# Revit family: Hager-WITTY ONE WALL MOUNTED-fr-BE-BE
name_source: partatom
category: Electrical Fixtures
units: mm (PartAtom-declared; Revit-internal decimal feet)

## family parameters
Always vertical = Yes
Cut with Voids When Loaded = No
Host = Wall
Maintain Annotation Orientation = No
OmniClass Number = 23.75.00.00
OmniClass Title = Climate Control (HVAC)
Part Type = Normal
Room Calculation Point = No
Round Connector Dimension = Use Diameter
Shared = No

## types (2) — shared parameters
BC_METADATA = {"ObjectGuid":"b7395028-ef9e-46b8-b49f-e0fe9c8fa070","ModelGuid":"b1efb829-c177-4a88-8b0d-f632edc25d22","VariantGuid":"c7b0c534-fef0-4725-a2d6-e8a658ebdb92","Revision":"#2","VariantName":"REF 1"}
BC_MODEL_ID = 1528865
BC_OBJECT_ID = 511137
BC_OBJECT_VERSION = #1
Code hager = ADD_EC002883_ECVS_WO
EF000003 - Type de montage = Montage mural
EF000008 - Largeur = 250 mm  [stored 0.82021 ft]
EF000040 - Hauteur = 370 mm  [stored 1.21391 ft]
EF000049 - Profondeur = 150 mm  [stored 0.492126 ft]
EF000458 - Avec affichage = No
EF001596 - Matériau du boîtier = Plastique
EF002136 - Puissance de raccordement nominale = 11000 W
EF003840 - Tension d'entrée = 400 V
EF004293 - Résistance aux chocs = IK08
EF005455 - Fréquence = 50/60 Hz
EF005474 - Classe de protection (IP) = IP54
EF007001 - Tension de sortie CC = 0 V
EF007353 - Courant de sortie max. CC = 0 A
EF009078 - Nombre de points de chargement = 1
EF009089 - Avec boîte de raccordement domestique = No
EF009300 - Puissance max. par point de chargement = 11000 W
EF009305 - Nombre de prises de charge type 2 = 1
EF009313 - Avec compteur d'énergie = No
EF009314 - Avec disjoncteur de protection = No
EF009547 - LTE = No
EF011072 - Compatible IFTTT = No
EF012191 - Avec lecteur de carte RFID intégré = Yes
EF012361 - NFC (Near Field Communication) = No
EF013154 - Connectable via Wi-Fi = No
EF014925 - Compatible avec Apple HomeKit = No
EF014926 - Compatible avec Google Assistant = No
EF014927 - Compatible avec Amazon Alexa = No
EF016385 - Standard radio 5G = No
EF017508 - Network-enabled as a master = No
EF017509 - DC residual current detection = Yes
EF017511 - With key switch = No
EF017512 - Export of charging logs = Yes
EF017513 - OpenChargePointProtocoll (OCPP) version = 1.6
EF017515 - Plug and charge (ISO 15118) = No
EF017517 - Network-enabled as an extender = No
EF017663 - Charging cable permanently lockable at charging device = Yes
EF017664 - Networkable via LAN = No
EF017665 - With MID compliant energy meter = No
EF017668 - Static load management integrated = No
EF017669 - Suitable for dynamic load management = Yes
EF017672 - Backend included = No
EF017972 - Operation and configuration by app = Yes
EF025053 - Finition raccordement côté installation = Triphasé
EFDE0066 - Calibration law compliant = No
ETIM class code = EC002883
ETIM class name = Charging device E-Mobility
HG000003-Range = WITTY ONE
HG000065-With socket TE = No
HG000099-Onfly Template ID = WittyOne_EVCS_Wall_Mounted
Manufacturer = hager France
Name = WITTY ONE WALL MOUNTED-BE
Name BIM&CO = Electricity
Name hager = ADD_ChargingStation_EC002883
Reference description = ECVS Witty 1x11kW 3P T2S
zero-valued in all types: Default Elevation, EF006577 - Nombre de prises CEE, EF008200 - Section de conducteur connectable, EF009091 - Nombre d'interrupteurs différentiels type A, EF009092 - Nombre d'interrupteurs différentiels type B, EF009301 - Nombre de coupleurs de charge type 1, EF009302 - Nombre de coupleurs de charge type 1 CCS, EF009303 - Nombre de coupleurs de charge type 2, EF009304 - Nombre de coupleurs de charge type 2 CCS, EF009306 - Nombre de coupleurs de charge GB CA, EF009307 - Nombre de coupleurs de charge GB CC, EF009308 - Nombre de prises de charge GB, EF009309 - Nombre de prises de charge type 3, EF009310 - Nombre de coupleurs de charge CHAdeMO, EF009311 - Nombre de prises de courant domestiques

## per-type parameters (varying)
| type | BC_VARIANT_ID | EF014895 - Longueur du câble de charge | HG000004-Manufacturer reference |
| WITTY ONE-1x11kW-3P-XVR111S-WALL MOUNTED | 1164618 | 0 mm  [stored 0 ft] | XVR111S |
| WITTY ONE-1x11kW-3P-XVR111C-WALL MOUNTED | 1164619 | 6500 mm  [stored 21.3255 ft] | XVR111C |

note: column(s) folded — value = type name in every type: Reference

note: [stored X ft] marks values corroborated as IEEE doubles in the binary element streams (Revit-internal decimal feet)
